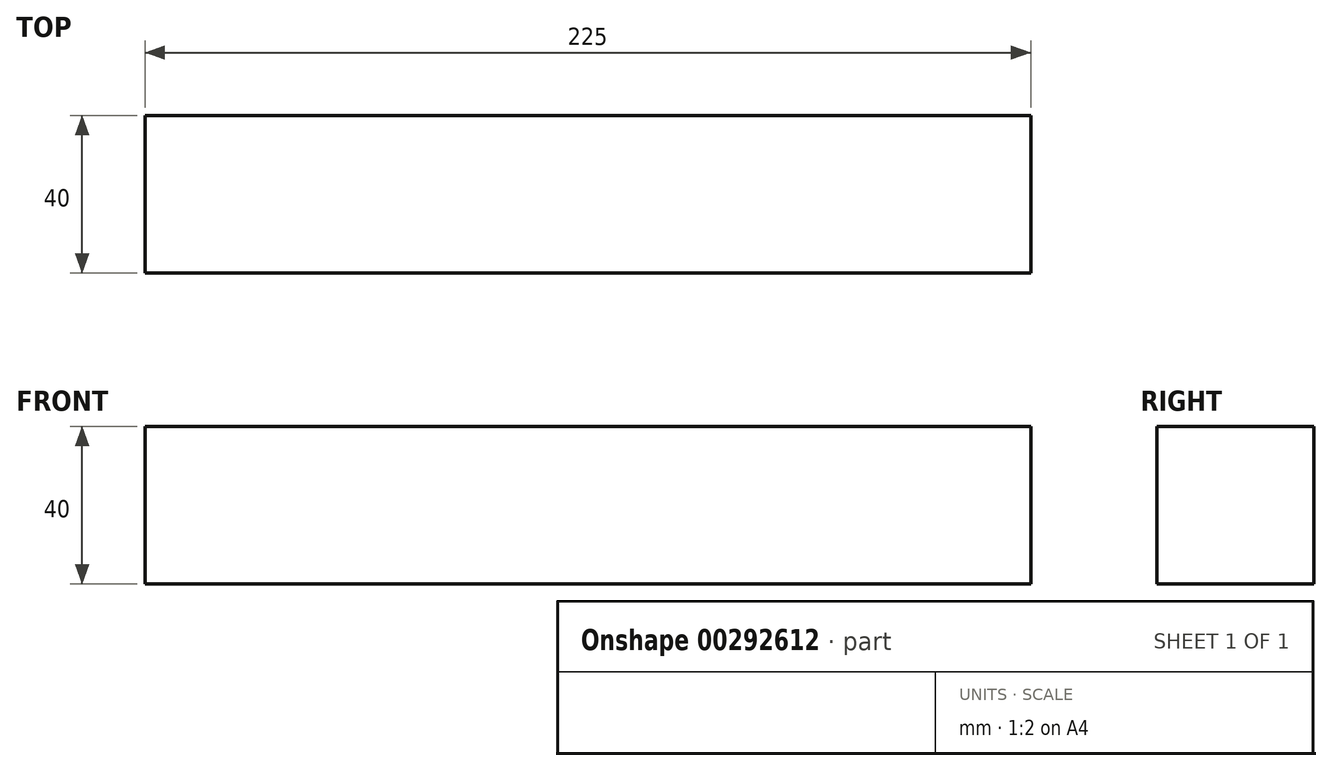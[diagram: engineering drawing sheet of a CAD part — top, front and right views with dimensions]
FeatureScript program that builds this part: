
annotation { "Feature Type Name" : "Feature", "Feature Type Description" : "" }
export const myFeature = defineFeature(function(context is Context, id is Id, definition is map)
    precondition{}
    {
        {
            var Q0;
            Q0=qCreatedBy(makeId("Front.planeOp"),FACE);
            var sketch = newSketch(context, id + "F0", { "sketchPlane" : qUnion([Q0])});
            skLineSegment(sketch, "E0", {"start": v(0, 40) * mm, "end": v(112.5, 40) * mm});
            skLineSegment(sketch, "E1", {"start": v(112.5, 40) * mm, "end": v(112.5, 0) * mm});
            skLineSegment(sketch, "E2.MirrorCS", {"start": v(0, 40) * mm, "end": v(-112.5, 40) * mm});
            skLineSegment(sketch, "E3.MirrorCS", {"start": v(-112.5, 40) * mm, "end": v(-112.5, 0) * mm});
            skLineSegment(sketch, "E4", {"start": v(-112.5, 0) * mm, "end": v(112.5, 0) * mm});
            skSolve(sketch);
        }
        {
            var Q0;
            Q0 = qSketchRegion(id + "F0", true);
            extrude(context, id + "F1", {"entities" : qUnion([Q0]), "endBound" : BoundingType.SYMMETRIC, "depth" : 40 * mm});
        }
    });
